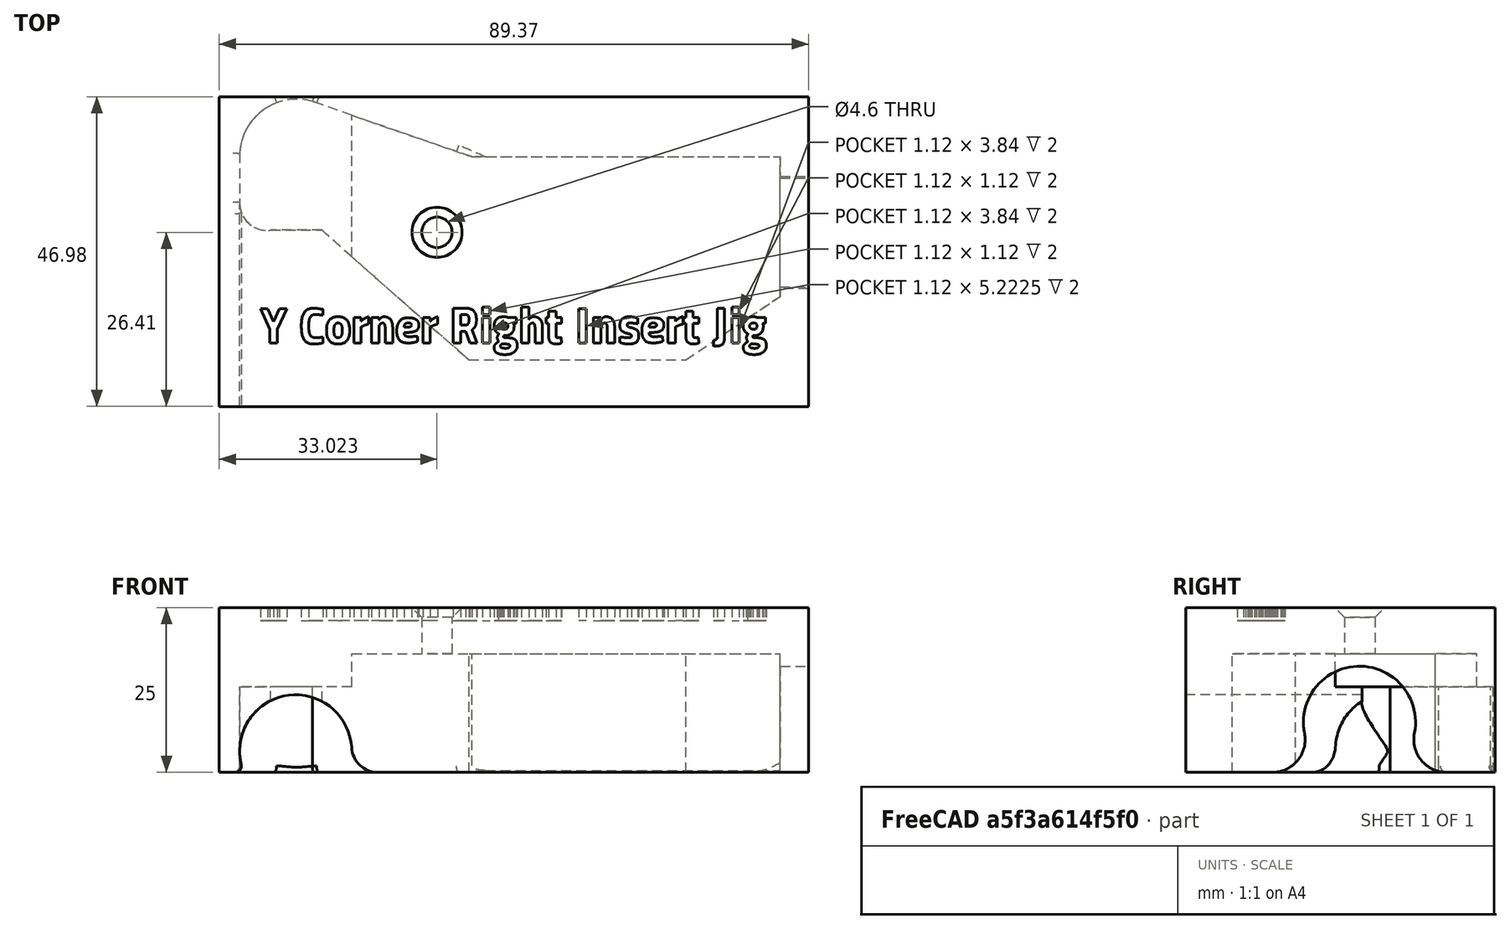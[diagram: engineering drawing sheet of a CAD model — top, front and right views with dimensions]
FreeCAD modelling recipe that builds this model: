
FCSTD DOCUMENT  (FreeCAD 0.17R9537 (Git))
Label: y_corner_right_insert_jig_m3
License: All rights reserved
LicenseURL: http://en.wikipedia.org/wiki/All_rights_reserved
objects: Sketcher::SketchObject×8, PartDesign::Pocket×6, PartDesign::Fillet×3, PartDesign::Body×2, Mesh::Feature×1, PartDesign::Pad×1, Part::Feature×1, PartDesign::Plane×1, PartDesign::Chamfer×1, Part::Mirroring×1, Part::Part2DObjectPython×1
note: 32 computed .brp shape members not serialized (recipe doc carries the construction recipe); baked Part::Feature solids carry a one-line shape summary decoded from their .brp

FEATURE [Mesh::Feature] y_corner_left_v2_4  label="y_corner_left_v2.4"
  Placement = pos=(-95,-15,-13) rot=(0,0,1;0rad)
FEATURE [Sketcher::SketchObject] Sketch
  MapMode = 5
  Support = -> [XY_Plane]
  sketch-geometry (4):
    g0: LineSegment StartX=-41.2454 StartY=-29.3641 StartZ=0 EndX=48.1248 EndY=-29.3641 EndZ=0
    g1: LineSegment StartX=48.1248 StartY=-29.3641 StartZ=0 EndX=48.1248 EndY=17.6233 EndZ=0
    g2: LineSegment StartX=48.1248 StartY=17.6233 StartZ=0 EndX=-41.2454 EndY=17.6233 EndZ=0
    g3: LineSegment StartX=-41.2454 StartY=17.6233 StartZ=0 EndX=-41.2454 EndY=-29.3641 EndZ=0
  constraints (8):
    c: Coincident(g0,g1)
    c: Coincident(g1,g2)
    c: Coincident(g2,g3)
    c: Coincident(g3,g0)
    c: Horizontal(g0)
    c: Horizontal(g2)
    c: Vertical(g1)
    c: Vertical(g3)
FEATURE [PartDesign::Pad] Pad
  Length = 25
  Length2 = 100
  Profile = -> Sketch
  Type = 0
FEATURE [Part::Feature] y_corner_left_v2_4001
  Placement = pos=(0,0,12) rot=(0,0,1;0rad)
  shape: bbox 81.06 x 37.98 x 18.29 mm, 18592 faces, 0 solids (baked)
FEATURE [Sketcher::SketchObject] Sketch001
  MapMode = 5
  Placement = pos=(0,0,0) rot=(1,0,0;3.14159rad)
  Support = -> [Pad]
  sketch-geometry (7):
    g0: LineSegment StartX=-21.1438 StartY=5.05934 StartZ=0 EndX=-3.38972 EndY=-10.5427 EndZ=0
    g1: LineSegment StartX=-3.38972 StartY=-10.5427 StartZ=0 EndX=29.5098 EndY=-10.5427 EndZ=0
    g2: LineSegment StartX=29.5098 StartY=-10.5427 StartZ=0 EndX=43.8429 EndY=-0.932231 EndZ=0
    g3: LineSegment StartX=43.8429 StartY=-0.932231 StartZ=0 EndX=43.8429 EndY=20.2526 EndZ=0
    g4: LineSegment StartX=-21.1438 StartY=5.05934 StartZ=0 EndX=-21.1438 EndY=26.5193 EndZ=0
    g5: LineSegment StartX=-21.1438 StartY=26.5193 StartZ=0 EndX=-2.94605 EndY=20.2526 EndZ=0
    g6: LineSegment StartX=-2.94605 StartY=20.2526 StartZ=0 EndX=43.8429 EndY=20.2526 EndZ=0
  constraints (11):
    c: Coincident(g1,g0)
    c: Horizontal(g1)
    c: Coincident(g2,g1)
    c: Coincident(g3,g2)
    c: Vertical(g3)
    c: Coincident(g4,g0)
    c: Vertical(g4)
    c: Coincident(g5,g4)
    c: Coincident(g6,g5)
    c: Coincident(g6,g3)
    c: Horizontal(g6)
FEATURE [PartDesign::Pocket] Pocket
  BaseFeature = -> Pad
  Length = 18
  Profile = -> Sketch001
  Type = 0
FEATURE [Sketcher::SketchObject] Sketch002
  ExternalGeometry = -> [Pocket]
  MapMode = 5
  Placement = pos=(0,0,0) rot=(1,0,0;3.14159rad)
  Support = -> [Pocket]
  sketch-geometry (7):
    g0: LineSegment StartX=-21.1438 StartY=5.05934 StartZ=0 EndX=-25.6743 EndY=9.11448 EndZ=0
    g1: LineSegment StartX=-25.6743 StartY=9.11448 StartZ=0 EndX=-33.4497 EndY=9.11448 EndZ=0
    g2: LineSegment StartX=-21.1438 StartY=26.5193 StartZ=0 EndX=-27.1407 EndY=28.6513 EndZ=0
    g3: ArcOfCircle CenterX=-29.5136 CenterY=20.3238 CenterZ=0 NormalX=0 NormalY=0 NormalZ=1 Radius=8.65904 StartAngle=1.2932 EndAngle=3.08945
    g4: LineSegment StartX=-38.1609 StartY=20.7751 StartZ=0 EndX=-38.1609 EndY=13.4153 EndZ=0
    g5: ArcOfCircle CenterX=-33.9785 CenterY=13.266 CenterZ=0 NormalX=0 NormalY=0 NormalZ=1 Radius=4.18506 StartAngle=3.10591 EndAngle=4.83908
    g6: LineSegment StartX=-21.1438 StartY=5.05934 StartZ=0 EndX=-21.1438 EndY=26.5193 EndZ=0
  constraints (11):
    c: Coincident(g0,g-3)
    c: Coincident(g1,g0)
    c: Horizontal(g1)
    c: Coincident(g2,g-3)
    c: Coincident(g3,g2)
    c: Coincident(g4,g3)
    c: Vertical(g4)
    c: Coincident(g1,g5)
    c: Coincident(g4,g5)
    c: Coincident(g6,g0)
    c: Coincident(g6,g2)
FEATURE [PartDesign::Pocket] Pocket001
  BaseFeature = -> Pocket
  Length = 13
  Profile = -> Sketch002
  Type = 0
FEATURE [Sketcher::SketchObject] Sketch003
  MapMode = 5
  Placement = pos=(0,17.6233,0) rot=(0,0.707107,0.707107;3.14159rad)
  Support = -> [Pocket001]
  sketch-geometry (1):
    g0: Circle CenterX=29.6574 CenterY=3.27274 CenterZ=0 NormalX=0 NormalY=0 NormalZ=1 Radius=8.5
  constraints (1):
    c: Radius(g0) = 8.5
FEATURE [PartDesign::Pocket] Pocket002
  BaseFeature = -> Pocket001
  Length = 35
  Profile = -> Sketch003
  Type = 0
FEATURE [Sketcher::SketchObject] Sketch004
  MapMode = 5
  Placement = pos=(48.1248,0,0) rot=(0.57735,0.57735,0.57735;2.0944rad)
  Support = -> [Pocket002]
  sketch-geometry (1):
    g0: Circle CenterX=-8.75085 CenterY=7.61123 CenterZ=0 NormalX=0 NormalY=0 NormalZ=1 Radius=8.5
  constraints (1):
    c: Radius(g0) = 8.5
FEATURE [PartDesign::Pocket] Pocket003
  BaseFeature = -> Pocket002
  Length = 5
  Profile = -> Sketch004
  Type = 0
FEATURE [PartDesign::Fillet] Fillet
  Base = -> Pocket003 [Edge31,Edge23]
  BaseFeature = -> Pocket003
  Radius = 5
FEATURE [PartDesign::Fillet] Fillet001
  Base = -> Fillet [Edge43]
  BaseFeature = -> Fillet
  Radius = 4
FEATURE [PartDesign::Fillet] Fillet002
  Base = -> Fillet001 [Edge32,Edge41,Edge40,Edge38,Edge37,Edge35]
  BaseFeature = -> Fillet001
  Radius = 1
FEATURE [Sketcher::SketchObject] Sketch005
  ExternalGeometry = -> [y_corner_left_v2_4001,Fillet002]
  MapMode = 5
  Placement = pos=(0,-29.3641,0) rot=(1,0,0;1.5708rad)
  Support = -> [Fillet002]
  sketch-geometry (1):
    g0: LineSegment StartX=-26.1602 StartY=0 StartZ=0 EndX=-26.1602 EndY=-0.999892 EndZ=0
  constraints (3):
    c: Coincident(g0,g-4)
    c: PointOnObject(g0,g-3)
    c: Vertical(g0)
FEATURE [Sketcher::SketchObject] Sketch006
  MapMode = 5
  Placement = pos=(0,0,18) rot=(1,0,0;3.14159rad)
  Support = -> [Fillet002]
  sketch-geometry (1):
    g0: Circle CenterX=-8.22724 CenterY=8.79045 CenterZ=0 NormalX=0 NormalY=0 NormalZ=1 Radius=2.3
  constraints (1):
    c: Radius(g0) = 2.3
FEATURE [PartDesign::Pocket] Pocket004
  BaseFeature = -> Fillet002
  Length = 5
  Profile = -> Sketch006
  Type = 1
FEATURE [PartDesign::Plane] DatumPlane
  MapMode = 5
  Placement = pos=(0,0,10) rot=(1,0,0;3.14159rad)
  Support = -> [Pocket004]
  superPlacement = pos=(0,0,-10) rot=(0,0,1;0rad)
FEATURE [Sketcher::SketchObject] Sketch007
  ExternalGeometry = -> [Pocket004]
  MapMode = 5
  Placement = pos=(0,17.6233,0) rot=(0,0.707107,0.707107;3.14159rad)
  Support = -> [Pocket004]
  sketch-geometry (1):
    g0: LineSegment StartX=3.2818 StartY=25 StartZ=0 EndX=3.2818 EndY=9.8977 EndZ=0
  constraints (2):
    c: PointOnObject(g0,g-3)
    c: Vertical(g0)
FEATURE [PartDesign::Chamfer] Chamfer
  Base = -> Pocket004 [Edge37]
  BaseFeature = -> Pocket004
  Size = 1.5
FEATURE [PartDesign::Body] Body
  Model = -> [Sketch,Pad,Sketch001,Pocket,Sketch002,Pocket001,Sketch003,Pocket002,Sketch004,Pocket003,Fillet,Fillet001,Fillet002,Pocket004,DatumPlane,Sketch007,Chamfer]
  Origin = -> BodyOrigin
FEATURE [Part::Mirroring] Part__Mirroring  label="Chamfer (Mirror #1)"
  Base = (0,0,0)
  Normal = (0,1,0)
  Source = -> Chamfer
FEATURE [Part::Part2DObjectPython] ShapeString  # Draft 2D object (typed FeaturePython)
  FontFile = <userpath>/Desktop/Titillium-BoldUpright.otf
  Placement = pos=(-35,-8,25) rot=(0,0,1;0rad)
  Size = 3
  String = Y Corner Right Insert Jig
  Support = -> [Part__Mirroring]
  Tracking = 55
FEATURE [PartDesign::Pocket] Pocket005
  BaseFeature = -> Part__Mirroring
  Length = 2
  Profile = -> ShapeString
  Type = 0
FEATURE [PartDesign::Body] Body001
  BaseFeature = -> Part__Mirroring
  Model = -> [Pocket005]
  Origin = -> Body001Origin
  Tip = -> Pocket005
